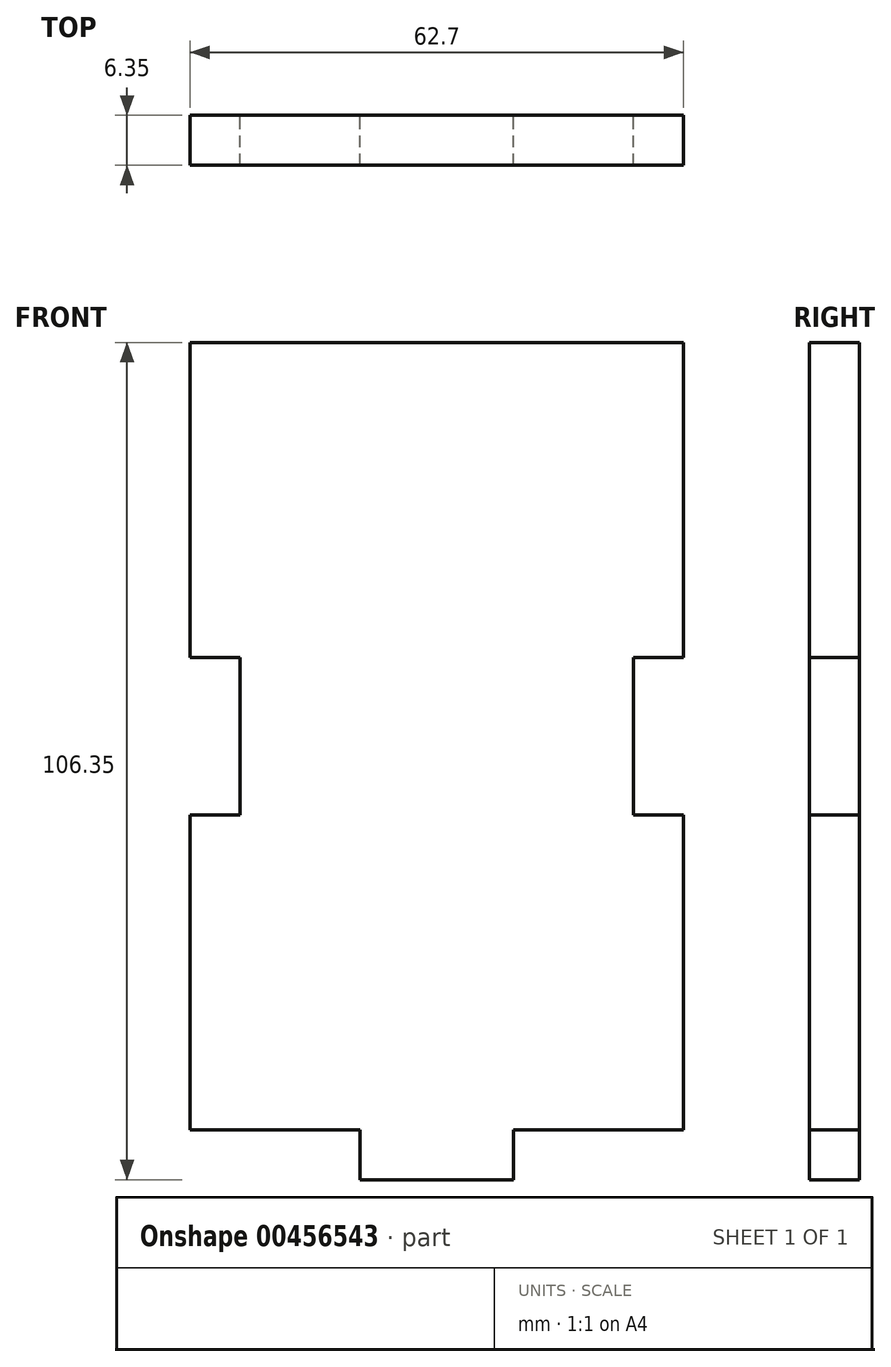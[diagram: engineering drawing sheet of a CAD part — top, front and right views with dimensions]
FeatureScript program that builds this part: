
annotation { "Feature Type Name" : "Feature", "Feature Type Description" : "" }
export const myFeature = defineFeature(function(context is Context, id is Id, definition is map)
    precondition{}
    {
        {
            var Q0;
            Q0=qCreatedBy(makeId("Front.planeOp"),FACE);
            var sketch = newSketch(context, id + "F0", { "sketchPlane" : qUnion([Q0])});
            skLineSegment(sketch, "E0.bottom", {"start": v(25, 50) * mm, "end": v(-25, 50) * mm});
            skLineSegment(sketch, "E0.top", {"start": v(25, -50) * mm, "end": v(-25, -50) * mm});
            skLineSegment(sketch, "E0.left", {"start": v(25, 50) * mm, "end": v(25, -50) * mm});
            skLineSegment(sketch, "E0.right", {"start": v(-25, 50) * mm, "end": v(-25, -50) * mm});
            skPoint(sketch, "E0.middle", {"position": v(0, 0) * mm});
            skLineSegment(sketch, "E1.bottom", {"start": v(-9.75, -50) * mm, "end": v(9.75, -50) * mm});
            skLineSegment(sketch, "E1.top", {"start": v(-9.75, -56.35) * mm, "end": v(9.75, -56.35) * mm});
            skLineSegment(sketch, "E1.left", {"start": v(-9.75, -50) * mm, "end": v(-9.75, -56.35) * mm});
            skLineSegment(sketch, "E1.right", {"start": v(9.75, -50) * mm, "end": v(9.75, -56.35) * mm});
            skLineSegment(sketch, "E2.bottom", {"start": v(25, 50) * mm, "end": v(31.35, 50) * mm});
            skLineSegment(sketch, "E2.top", {"start": v(25, 10) * mm, "end": v(31.35, 10) * mm});
            skLineSegment(sketch, "E2.left", {"start": v(25, 50) * mm, "end": v(25, 10) * mm});
            skLineSegment(sketch, "E2.right", {"start": v(31.35, 50) * mm, "end": v(31.35, 10) * mm});
            skLineSegment(sketch, "E3.bottom", {"start": v(25, -50) * mm, "end": v(31.35, -50) * mm});
            skLineSegment(sketch, "E3.top", {"start": v(25, -10) * mm, "end": v(31.35, -10) * mm});
            skLineSegment(sketch, "E3.left", {"start": v(25, -50) * mm, "end": v(25, -10) * mm});
            skLineSegment(sketch, "E3.right", {"start": v(31.35, -50) * mm, "end": v(31.35, -10) * mm});
            skLineSegment(sketch, "E4.bottom", {"start": v(-25, -50) * mm, "end": v(-31.35, -50) * mm});
            skLineSegment(sketch, "E4.top", {"start": v(-25, -10) * mm, "end": v(-31.35, -10) * mm});
            skLineSegment(sketch, "E4.left", {"start": v(-25, -50) * mm, "end": v(-25, -10) * mm});
            skLineSegment(sketch, "E4.right", {"start": v(-31.35, -50) * mm, "end": v(-31.35, -10) * mm});
            skLineSegment(sketch, "E5.bottom", {"start": v(-25, 50) * mm, "end": v(-31.35, 50) * mm});
            skLineSegment(sketch, "E5.top", {"start": v(-25, 10) * mm, "end": v(-31.35, 10) * mm});
            skLineSegment(sketch, "E5.left", {"start": v(-25, 50) * mm, "end": v(-25, 10) * mm});
            skLineSegment(sketch, "E5.right", {"start": v(-31.35, 50) * mm, "end": v(-31.35, 10) * mm});
            skSolve(sketch);
        }
        {
            var Q0;
            Q0 = qSketchRegion(id + "F0", true);
            extrude(context, id + "F1", {"entities" : qUnion([Q0]), "depth" : 6.35 * mm});
        }
    });
